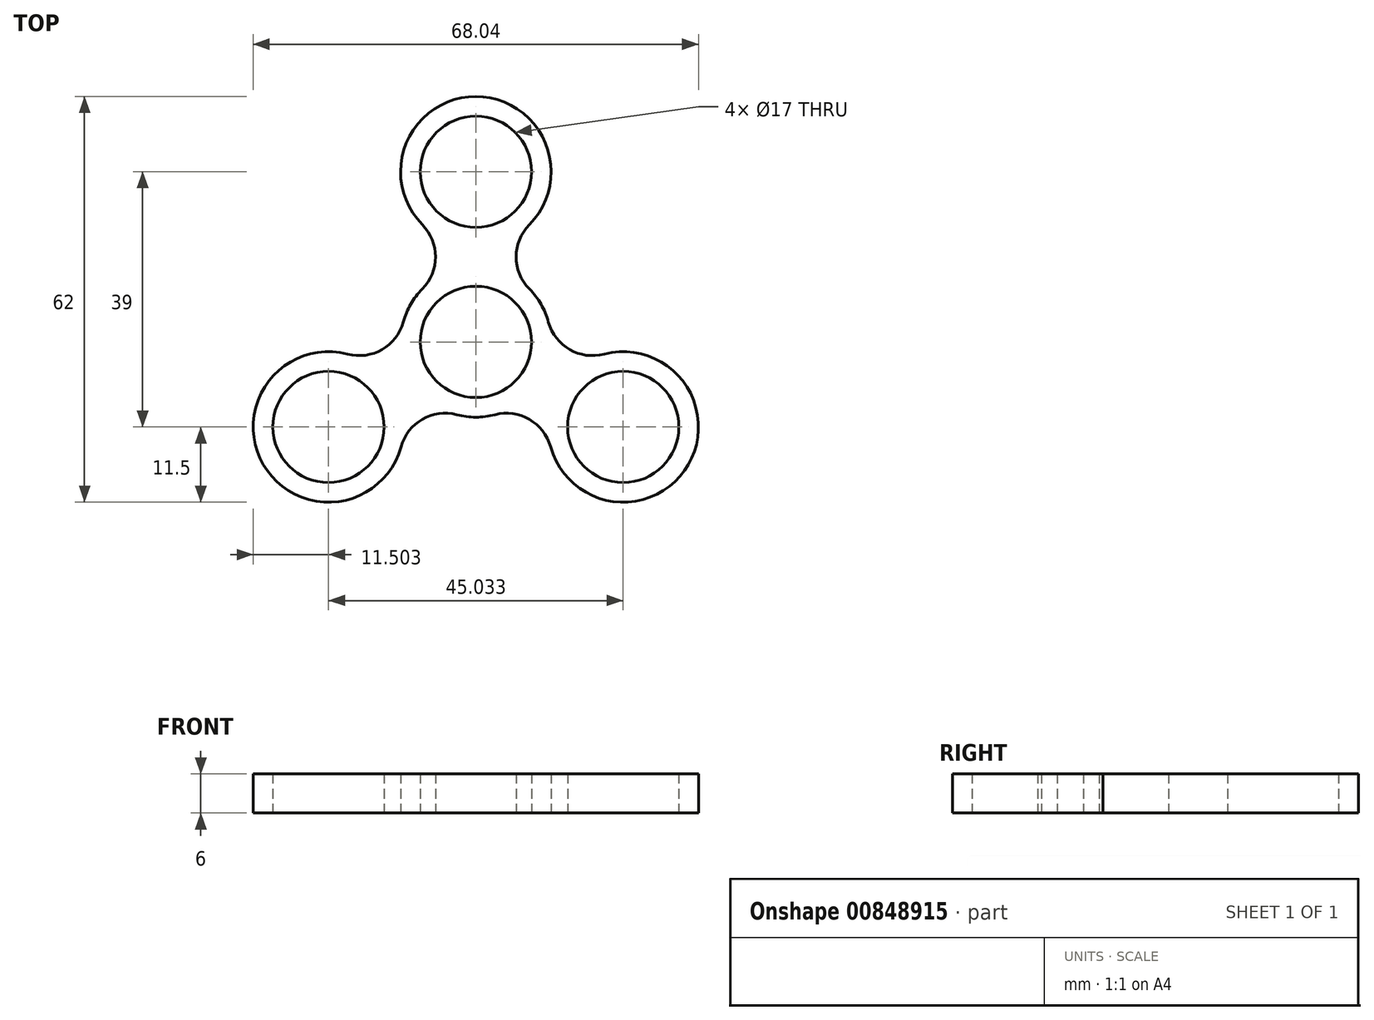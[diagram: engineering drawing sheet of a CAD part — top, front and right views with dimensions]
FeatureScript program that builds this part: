
annotation { "Feature Type Name" : "Feature", "Feature Type Description" : "" }
export const myFeature = defineFeature(function(context is Context, id is Id, definition is map)
    precondition{}
    {
        {
            var Q0;
            Q0=qCreatedBy(makeId("Top.planeOp"),FACE);
            var sketch = newSketch(context, id + "F0", { "sketchPlane" : qUnion([Q0])});
            skCircle(sketch, "E0", {"center": v(0, 0) * mm, "radius": 8.5 * mm});
            skCircle(sketch, "E1", {"center": v(0, 26) * mm, "radius": 8.5 * mm});
            skLineSegment(sketch, "E2", {"start": v(0, 0) * mm, "end": v(0, 26) * mm, "construction": true});
            skCircle(sketch, "E3", {"center": v(0, 26) * mm, "radius": 11.5 * mm});
            skCircle(sketch, "E4", {"center": v(0, 0) * mm, "radius": 11.5 * mm});
            skArc(sketch, "E5", {"start": v(-8.18, 8.08) * mm, "mid": v(-6.16, 13) * mm, "end": v(-8.18, 17.92) * mm});
            skArc(sketch, "E6.MirrorCS", {"start": v(8.18, 8.08) * mm, "mid": v(6.16, 13) * mm, "end": v(8.18, 17.92) * mm});
            skArc(sketch, "E7.1.0", {"start": v(-2.9, -11.13) * mm, "mid": v(-8.18, -11.84) * mm, "end": v(-11.43, -16.05) * mm});
            skCircle(sketch, "E7.1.1", {"center": v(-22.52, -13) * mm, "radius": 11.5 * mm});
            skArc(sketch, "E7.1.2", {"start": v(-11.09, 3.05) * mm, "mid": v(-14.34, -1.16) * mm, "end": v(-19.6, -1.87) * mm});
            skCircle(sketch, "E7.1.3", {"center": v(-22.52, -13) * mm, "radius": 8.5 * mm});
            skArc(sketch, "E7.2.0", {"start": v(11.09, 3.05) * mm, "mid": v(14.34, -1.16) * mm, "end": v(19.6, -1.87) * mm});
            skCircle(sketch, "E7.2.1", {"center": v(22.52, -13) * mm, "radius": 11.5 * mm});
            skArc(sketch, "E7.2.2", {"start": v(2.9, -11.13) * mm, "mid": v(8.18, -11.84) * mm, "end": v(11.43, -16.05) * mm});
            skCircle(sketch, "E7.2.3", {"center": v(22.52, -13) * mm, "radius": 8.5 * mm});
            skCircle(sketch, "E8", {"center": v(0, 0) * mm, "radius": 37.5 * mm, "construction": true});
            skSolve(sketch);
        }
        {
            var Q0;
            Q0=makeQuery(id+"F0.imprint","IMPRINT",FACE,{"disambiguationData":[TD([[makeQuery(id+"F0.imprint","IMPRINT",EDGE,{"derivedFrom":sQuery(id+"F0.wireOp",EDGE,"E1")}),-1.0]])]});
            var Q1;
            {var subQ0=sQuery(id+"F0.wireOp",EDGE,"E5");Q1=makeQuery(id+"F0.imprint","IMPRINT",FACE,{"disambiguationData":[TD([[makeQuery(id+"F0.imprint","IMPRINT",EDGE,{"derivedFrom":subQ0}),-1.0]])]});}
            var Q2;
            Q2=makeQuery(id+"F0.imprint","IMPRINT",FACE,{"disambiguationData":[TD([[makeQuery(id+"F0.imprint","IMPRINT",EDGE,{"derivedFrom":sQuery(id+"F0.wireOp",EDGE,"E0")}),-1.0]])]});
            var Q3;
            {var subQ0=sQuery(id+"F0.wireOp",EDGE,"E7.1.0");Q3=makeQuery(id+"F0.imprint","IMPRINT",FACE,{"disambiguationData":[TD([[makeQuery(id+"F0.imprint","IMPRINT",EDGE,{"derivedFrom":subQ0}),-1.0]])]});}
            var Q4;
            Q4=makeQuery(id+"F0.imprint","IMPRINT",FACE,{"disambiguationData":[TD([[makeQuery(id+"F0.imprint","IMPRINT",EDGE,{"derivedFrom":sQuery(id+"F0.wireOp",EDGE,"E7.1.3")}),-1.0]])]});
            var Q5;
            {var subQ0=sQuery(id+"F0.wireOp",EDGE,"E7.2.0");Q5=makeQuery(id+"F0.imprint","IMPRINT",FACE,{"disambiguationData":[TD([[makeQuery(id+"F0.imprint","IMPRINT",EDGE,{"derivedFrom":subQ0}),-1.0]])]});}
            var Q6;
            Q6=makeQuery(id+"F0.imprint","IMPRINT",FACE,{"disambiguationData":[TD([[makeQuery(id+"F0.imprint","IMPRINT",EDGE,{"derivedFrom":sQuery(id+"F0.wireOp",EDGE,"E7.2.3")}),-1.0]])]});
            extrude(context, id + "F1", {"entities" : qUnion([Q0, Q1, Q2, Q3, Q4, Q5, Q6]), "depth" : 6 * mm, "offsetDistance" : 25 * mm});
        }
    });
